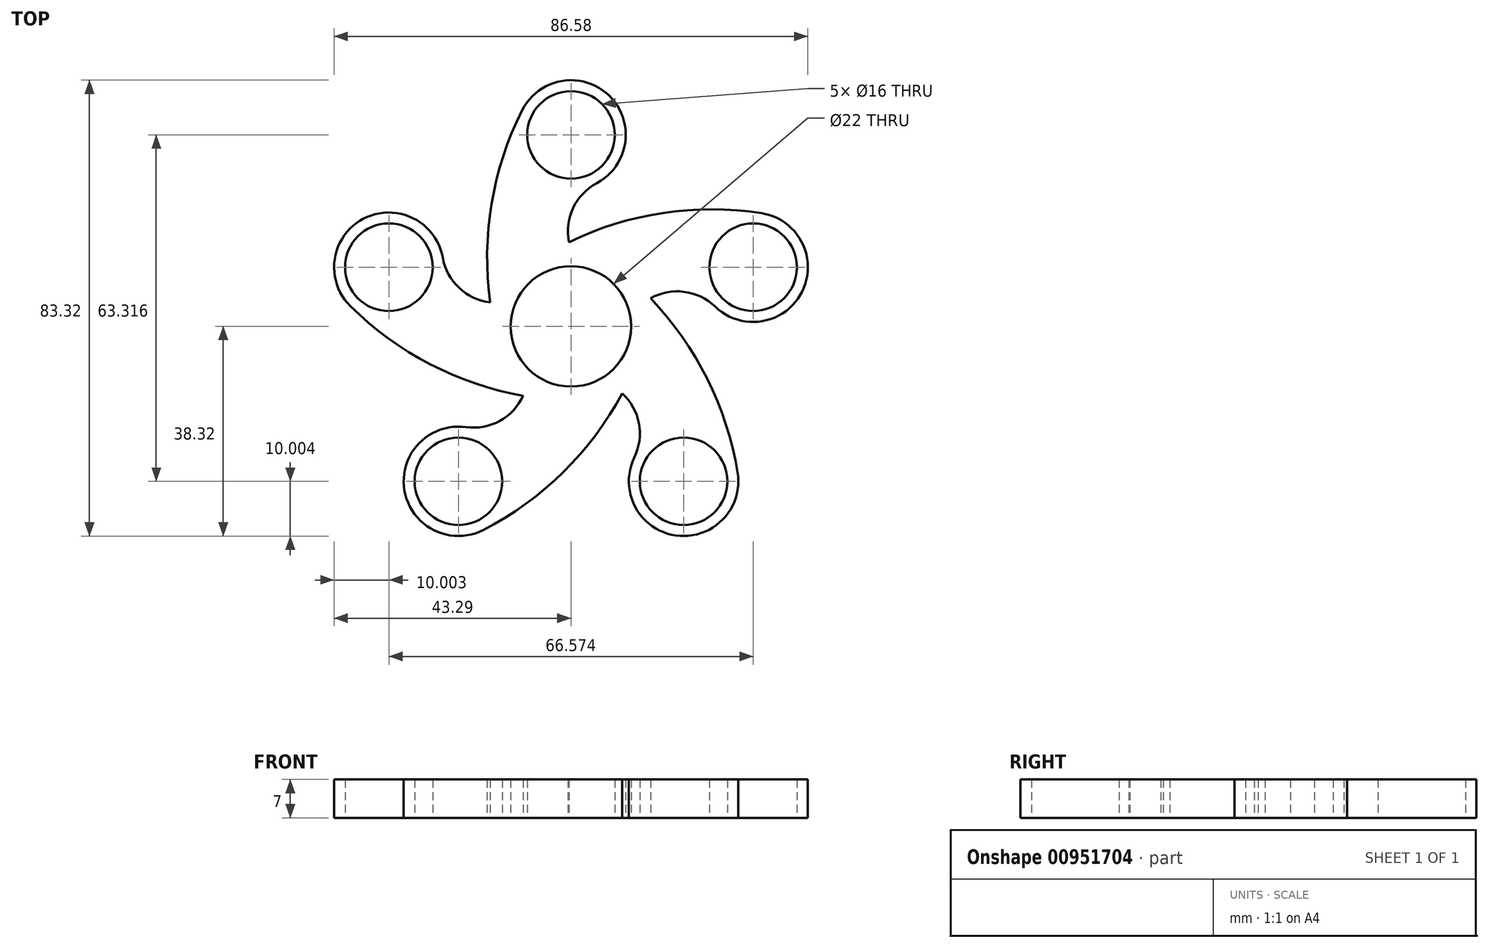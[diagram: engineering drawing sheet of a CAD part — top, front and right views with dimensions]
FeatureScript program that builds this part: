
annotation { "Feature Type Name" : "Feature", "Feature Type Description" : "" }
export const myFeature = defineFeature(function(context is Context, id is Id, definition is map)
    precondition{}
    {
        {
            assignVariable(context, id + "F0", {"name" : "number_of_arms", "anyValue" : 5});
        }
        {
            var Q0;
            Q0=qCreatedBy(makeId("Top.planeOp"),FACE);
            var sketch = newSketch(context, id + "F1", { "sketchPlane" : qUnion([Q0])});
            skCircle(sketch, "E0", {"center": v(0, 0) * mm, "radius": 11 * mm});
            skCircle(sketch, "E1", {"center": v(0, 0) * mm, "radius": 14 * mm});
            skCircle(sketch, "E2", {"center": v(0, 35) * mm, "radius": 8 * mm});
            skCircle(sketch, "E3", {"center": v(0, 35) * mm, "radius": 10 * mm});
            skArc(sketch, "E4", {"start": v(-8.93, 39.5) * mm, "mid": v(-14.84, 20.18) * mm, "end": v(-14, 0) * mm});
            skArc(sketch, "E5", {"start": v(4.7, 26.18) * mm, "mid": v(0.1, 20.96) * mm, "end": v(0, 14) * mm});
            skSolve(sketch);
        }
        {
            var Q0;
            Q0 = qSketchRegion(id + "F1", true);
            extrude(context, id + "F2", {"entities" : qUnion([Q0]), "depth" : 7 * mm, "offsetDistance" : 25 * mm});
        }
        {
            var Q0;
            Q0=makeQuery(id+"F2.opExtrude","SWEPT_BODY",BODY,{"disambiguationData":[OSD([sQuery(id+"F1.wireOp",EDGE,"E0"),sQuery(id+"F1.wireOp",EDGE,"E1"),sQuery(id+"F1.wireOp",EDGE,"E2"),sQuery(id+"F1.wireOp",EDGE,"E3"),sQuery(id+"F1.wireOp",EDGE,"E4"),sQuery(id+"F1.wireOp",EDGE,"E5")])]});
            var Q1;
            Q1=makeQuery(id+"F2.opExtrude","CAP_EDGE",EDGE,{"disambiguationData":[OSD([sQuery(id+"F1.wireOp",EDGE,"E0")])],"isStart":false});
            circularPattern(context, id + "F3", {"operationType" : NewBodyOperationType.ADD, "entities" : qUnion([Q0]), "axis" : qUnion([Q1]), "angle" : 360 * degree, "instanceCount" : getVariable(context, 'number_of_arms'), "equalSpace" : true});
        }
    });
